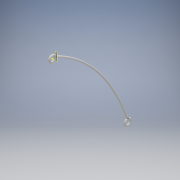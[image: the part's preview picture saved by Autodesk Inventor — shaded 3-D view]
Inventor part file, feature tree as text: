
AUTODESK INVENTOR PART (.ipt)
format: ipt  version: 2018 (Build 220112000, 112)  size: 155,648 bytes
history: native  units: mm
features: sketch x5, plane x3, revolve x2, sweep x1
ambient origin geometry x8: Origin, YZ Plane, XZ Plane, XY Plane, X Axis, Y Axis, Z Axis, Center Point
bodies: Solid1 (feature_tree)
feature tree (11):
  revolve  "Revolution1"  Angle=90.0deg
  sketch  "Sketch2"  dims[d2=400.0mm d3=40.0mm d4=20.0mm]
  plane  "Work Plane1"
  plane  "Work Plane2"
  sweep  "Sweep1"
  plane  "Work Plane3"
  revolve  "Revolution2"  [1 undecoded]
  sketch  "Sketch1"  dims[d0=20.0mm d1=90.0deg]
  sketch  "Sketch3"  dims[d5=0.0mm d6=0.0mm d7=800.0mm]
  sketch  "Sketch4"  dims[d8=20.0mm]
  sketch  "Sketch5"  dims[d9=90.0deg]
note: 1 required parameter value undecoded (feature->parameter linkage not recoverable at this tier; creation-order binding heuristic only, values carry confidence <= 0.55)
